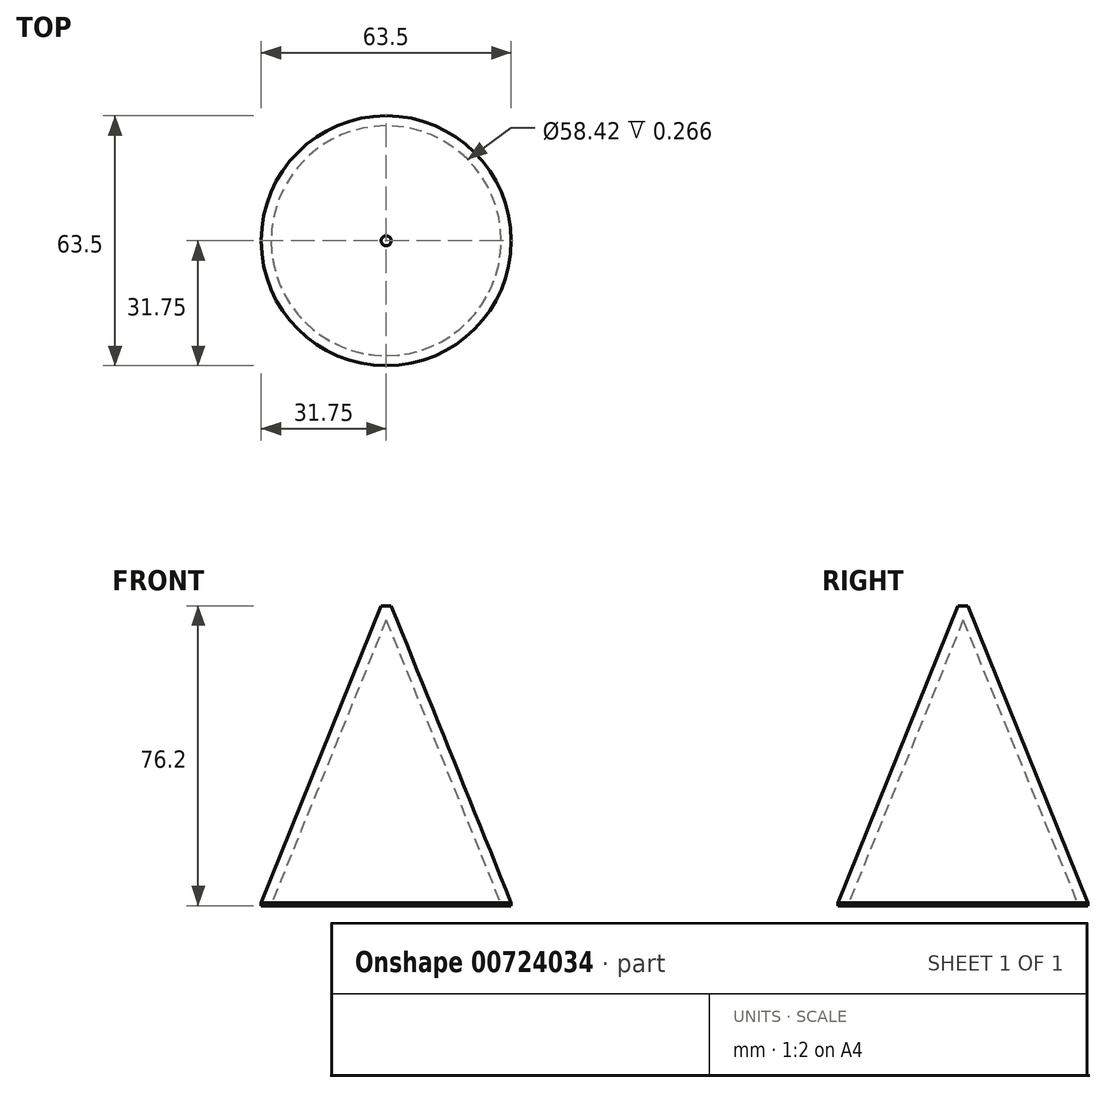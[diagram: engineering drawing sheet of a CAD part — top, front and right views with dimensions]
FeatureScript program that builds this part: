
annotation { "Feature Type Name" : "Feature", "Feature Type Description" : "" }
export const myFeature = defineFeature(function(context is Context, id is Id, definition is map)
    precondition{}
    {
        {
            var Q0;
            Q0=qCreatedBy(makeId("Top.planeOp"),FACE);
            var sketch = newSketch(context, id + "F0", { "sketchPlane" : qUnion([Q0])});
            skCircle(sketch, "E0", {"center": v(0, 0) * mm, "radius": 31.75 * mm});
            skSolve(sketch);
        }
        {
            var Q0;
            Q0 = qSketchRegion(id + "F0", true);
            extrude(context, id + "F1", {"entities" : qUnion([Q0]), "depth" : 76.2 * mm, "offsetDistance" : 25.4 * mm});
        }
        {
            var Q0;
            Q0=makeQuery(id+"F1.opExtrude","CAP_FACE",FACE,{"disambiguationData":[OSD([sQuery(id+"F0.wireOp",EDGE,"E0")])],"isStart":false});
            chamfer(context, id + "F2", {"entities" : qUnion([Q0]), "chamferType" : ChamferType.OFFSET_ANGLE, "width" : 30.48 * mm, "oppositeDirection" : false, "angle" : 68 * degree, "tangentPropagation" : true});
        }
        {
            var Q0;
            Q0=makeQuery(id+"F1.opExtrude","CAP_FACE",FACE,{"disambiguationData":[OSD([sQuery(id+"F0.wireOp",EDGE,"E0")])],"isStart":true});
            shell(context, id + "F3", {"entities" : qUnion([Q0]), "thickness" : 2.54 * mm});
        }
    });
